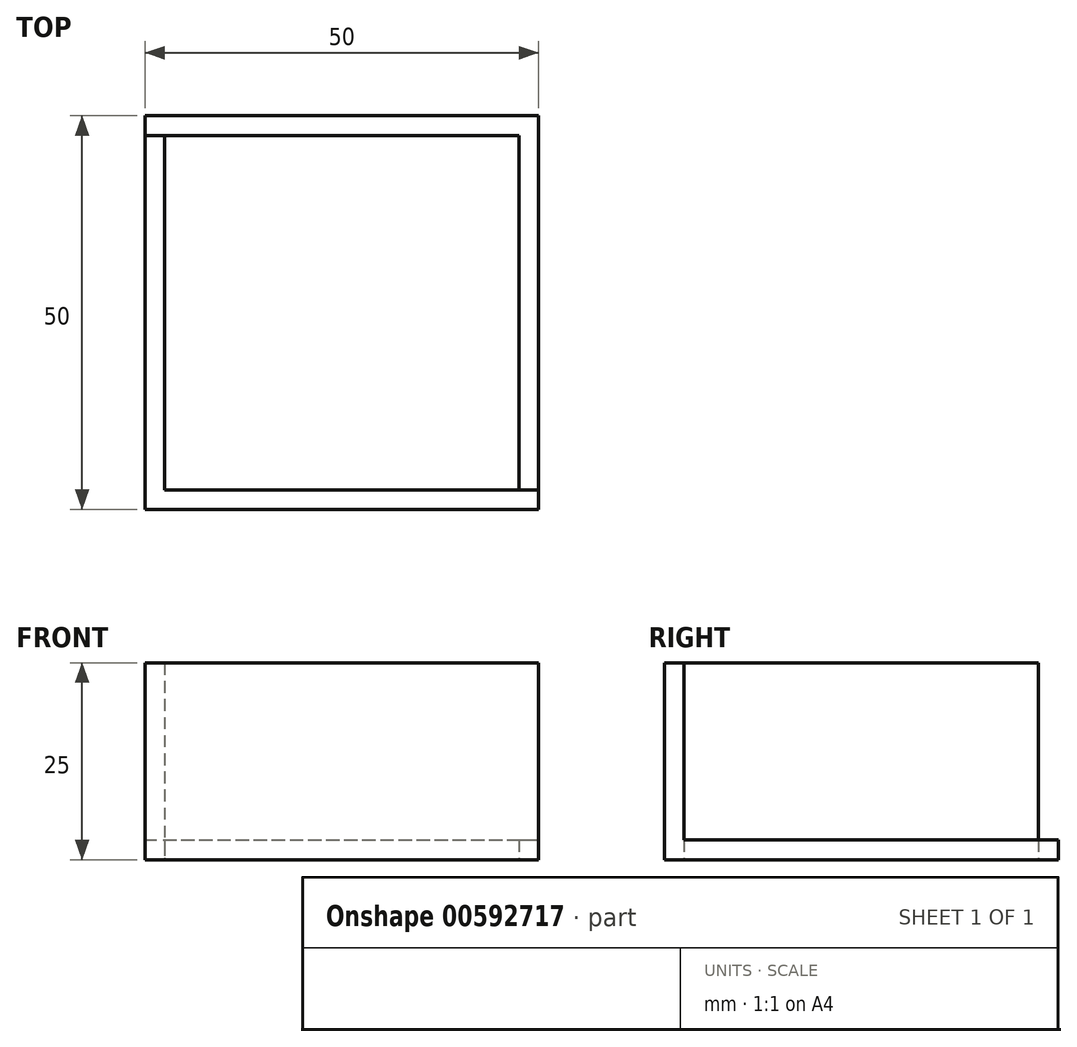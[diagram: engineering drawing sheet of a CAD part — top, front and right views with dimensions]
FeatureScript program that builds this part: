
annotation { "Feature Type Name" : "Feature", "Feature Type Description" : "" }
export const myFeature = defineFeature(function(context is Context, id is Id, definition is map)
    precondition{}
    {
        {
            var Q0;
            Q0=qCreatedBy(makeId("Top.planeOp"),FACE);
            var sketch = newSketch(context, id + "F0", { "sketchPlane" : qUnion([Q0])});
            skLineSegment(sketch, "E0.bottom", {"start": v(-24.64, 31.26) * mm, "end": v(25.36, 31.26) * mm});
            skLineSegment(sketch, "E0.top", {"start": v(-24.64, -18.74) * mm, "end": v(25.36, -18.74) * mm});
            skLineSegment(sketch, "E0.left", {"start": v(-24.64, 31.26) * mm, "end": v(-24.64, -18.74) * mm});
            skLineSegment(sketch, "E0.right", {"start": v(25.36, 31.26) * mm, "end": v(25.36, -18.74) * mm});
            skSolve(sketch);
        }
        {
            var Q0;
            Q0=makeQuery(id+"F0.imprint","IMPRINT",FACE,{"disambiguationData":[TD([[makeQuery(id+"F0.imprint","IMPRINT",EDGE,{"derivedFrom":sQuery(id+"F0.wireOp",EDGE,"E0.bottom")}),-1.0]])]});
            extrude(context, id + "F1", {"entities" : qUnion([Q0]), "depth" : 25 * mm, "offsetDistance" : 25 * mm});
        }
        {
            var Q0;
            Q0=makeQuery(id+"F1.opExtrude","CAP_FACE",FACE,{"disambiguationData":[OSD([sQuery(id+"F0.wireOp",EDGE,"E0.bottom"),sQuery(id+"F0.wireOp",EDGE,"E0.top"),sQuery(id+"F0.wireOp",EDGE,"E0.left"),sQuery(id+"F0.wireOp",EDGE,"E0.right")])],"isStart":false});
            var Q1;
            Q1=makeQuery(id+"F1.opExtrude","CAP_FACE",FACE,{"disambiguationData":[OSD([sQuery(id+"F0.wireOp",EDGE,"E0.bottom"),sQuery(id+"F0.wireOp",EDGE,"E0.top"),sQuery(id+"F0.wireOp",EDGE,"E0.left"),sQuery(id+"F0.wireOp",EDGE,"E0.right")])],"isStart":true});
            shell(context, id + "F2", {"entities" : qUnion([Q0, Q1]), "thickness" : 2.5 * mm});
        }
        {
            var Q0;
            Q0=makeQuery(id+"F1.opExtrude","CAP_FACE",FACE,{"disambiguationData":[OSD([sQuery(id+"F0.wireOp",EDGE,"E0.bottom"),sQuery(id+"F0.wireOp",EDGE,"E0.top"),sQuery(id+"F0.wireOp",EDGE,"E0.left"),sQuery(id+"F0.wireOp",EDGE,"E0.right")])],"isStart":false});
            var Q1;
            Q1=makeQuery(id+"F2.opShell","OFFSET_FACE",FACE,{"disambiguationData":[OSD([sQuery(id+"F0.wireOp",EDGE,"E0.bottom")])]});
            var Q2;
            Q2=makeQuery(id+"F2.opShell","OFFSET_FACE",FACE,{"disambiguationData":[OSD([sQuery(id+"F0.wireOp",EDGE,"E0.right")])]});
            var Q3;
            Q3=makeQuery(id+"F1.opExtrude","SWEPT_FACE",FACE,{"disambiguationData":[OSD([sQuery(id+"F0.wireOp",EDGE,"E0.right")])]});
            var Q4;
            Q4=makeQuery(id+"F1.opExtrude","SWEPT_FACE",FACE,{"disambiguationData":[OSD([sQuery(id+"F0.wireOp",EDGE,"E0.bottom")])]});
            var Q5;
            Q5=makeQuery(id+"F2.opShell","OFFSET_FACE",FACE,{"disambiguationData":[OSD([sQuery(id+"F0.wireOp",EDGE,"E0.top")])]});
            var Q6;
            Q6=makeQuery(id+"F1.opExtrude","SWEPT_FACE",FACE,{"disambiguationData":[OSD([sQuery(id+"F0.wireOp",EDGE,"E0.left")])]});
            shell(context, id + "F3", {"entities" : qUnion([Q0, Q1, Q2, Q3, Q4, Q5, Q6]), "thickness" : 2.5 * mm});
        }
    });
